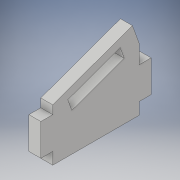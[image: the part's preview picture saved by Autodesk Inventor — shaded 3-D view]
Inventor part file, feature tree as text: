
AUTODESK INVENTOR PART (.ipt)
format: ipt  version: 2017 (Build 210142000, 142)  size: 121,344 bytes
history: native  units: in
note: dims shown in document units (in); Inventor stores cm internally (conversion verified against a paired STEP export)
features: extrude x1, sketch x1
ambient origin geometry x8: Origin, YZ Plane, XZ Plane, XY Plane, X Axis, Y Axis, Z Axis, Center Point
bodies: Body1 (feature_tree)
feature tree (2):
  extrude  "Extrusion1"  Depth=0.0787in
  sketch  "Sketch2"  dims[d9=0.1969in d11=0.0787in d12=0.1969in d13=0.1575in d14=0.1575in d15=0.5512in d16=0.2756in d17=0.1181in d18=0.1181in d21=0.1181in d22=0.1181in d23=0.1181in d24=0.0in d27=0.8547in d28=0.315in d29=0.315in]
